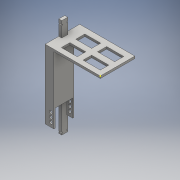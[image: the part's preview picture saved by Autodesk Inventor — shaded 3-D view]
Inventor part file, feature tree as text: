
AUTODESK INVENTOR PART (.ipt)
format: ipt  version: 2016 (Build 200138000, 138)  size: 315,904 bytes
history: native  units: mm
features: sketch x15, extrude x13, hole x1
ambient origin geometry x8: Origin, YZ Plane, XZ Plane, XY Plane, X Axis, Y Axis, Z Axis, Center Point
bodies: Body1 (feature_tree), Body2 (feature_tree), Body3 (feature_tree), Body4 (feature_tree), Body5 (feature_tree)
feature tree (29):
  extrude  "Extrusion2"  Depth=70.0mm
  extrude  "Extrusion3"  Depth=27.0mm TaperAngle=0.0deg
  extrude  "Extrusion4"  Depth=24.0mm
  extrude  "Extrusion5"  Depth=1.5mm
  extrude  "Extrusion6"  Depth=53.0mm
  sketch  "Sketch11"  dims[d46=32.0mm d47=7.0mm]
  hole  "Hole2"  [1 undecoded]
  extrude  "Extrusion7"  Depth=10.0mm TaperAngle=0.0deg
  extrude  "Extrusion8"  Depth=8.0mm
  extrude  "Extrusion9"  Depth=3.0mm
  extrude  "Extrusion10"  Depth=4.25mm
  extrude  "Extrusion11"  Depth=6.0mm
  extrude  "Extrusion12"  Depth=6.0mm
  extrude  "Extrusion13"  Depth=4.25mm
  extrude  "Extrusion14"  Depth=6.0mm
  sketch  "Sketch3"  dims[d26=70.0mm d27=70.0mm]
  sketch  "Sketch4"  dims[d29=6.0mm d31=27.0mm d32=0.0mm]
  sketch  "Sketch5"  dims[d34=20.0mm d35=0.0mm d36=24.0mm]
  sketch  "Sketch9"  dims[d37=24.0mm d38=1.5mm]
  sketch  "Sketch10"  dims[d39=10.0mm d40=0.0mm d45=53.0mm]
  sketch  "Sketch12"  dims[d48=7.0mm d49=10.0mm d50=0.0mm]
  sketch  "Sketch15"  dims[d51=8.0mm d52=8.0mm]
  sketch  "Sketch18"  dims[d53=3.0mm d54=0.0mm d55=4.25mm]
  sketch  "Sketch19"  dims[d56=4.25mm d57=4.25mm]
  sketch  "Sketch20"  dims[d59=6.0mm d60=6.0mm]
  sketch  "Sketch21"  dims[d61=6.0mm d62=4.25mm]
  sketch  "Sketch22"  dims[d63=4.25mm d64=4.25mm]
  sketch  "Sketch23"  dims[d65=6.0mm d66=6.0mm]
  sketch  "Sketch24"  dims[d67=6.0mm d68=4.25mm d69=6.0mm d70=4.0mm d71=2.0mm d72=90.0deg d73=8.0mm d74=0.0mm d75=3.0mm d76=0.0mm d77=1.0mm d78=0.0mm d79=1.0mm d80=0.0mm d81=20.5mm d82=94.0mm d83=20.5mm d84=180.0deg d85=2.0mm d86=0.0mm d87=2.0mm d88=0.0mm d89=2.0mm d90=0.0mm d91=2.0mm d92=0.0mm d93=17.5mm d94=1.5mm d95=1.0mm d96=2.0mm d97=0.0mm]
note: 1 required parameter value undecoded (feature->parameter linkage not recoverable at this tier; creation-order binding heuristic only, values carry confidence <= 0.55)
